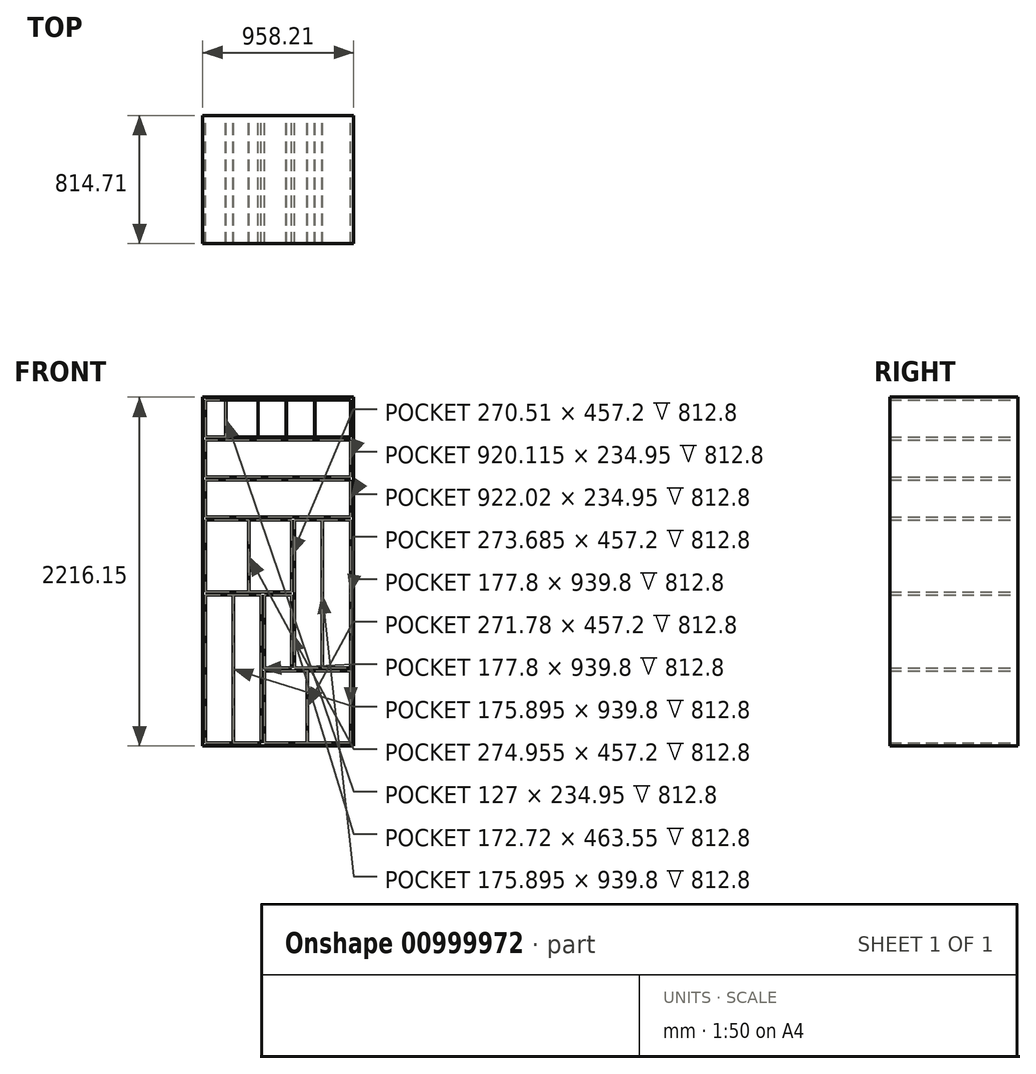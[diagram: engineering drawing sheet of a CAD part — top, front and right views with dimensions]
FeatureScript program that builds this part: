
annotation { "Feature Type Name" : "Feature", "Feature Type Description" : "" }
export const myFeature = defineFeature(function(context is Context, id is Id, definition is map)
    precondition{}
    {
        {
            var Q0;
            Q0=qCreatedBy(makeId("Front.planeOp"),FACE);
            var sketch = newSketch(context, id + "F0", { "sketchPlane" : qUnion([Q0])});
            skLineSegment(sketch, "E0.bottom", {"start": v(-388.07, -1236.82) * mm, "end": v(532.05, -1236.82) * mm});
            skLineSegment(sketch, "E0.left", {"start": v(-388.07, -1236.82) * mm, "end": v(-388.07, -436.72) * mm});
            skLineSegment(sketch, "E1.top", {"start": v(-388.07, 452.28) * mm, "end": v(533.95, 452.28) * mm});
            skLineSegment(sketch, "E1.left", {"start": v(-388.07, -436.72) * mm, "end": v(-388.07, 452.28) * mm});
            skLineSegment(sketch, "E1.right", {"start": v(533.95, -436.72) * mm, "end": v(533.95, 452.28) * mm});
            skLineSegment(sketch, "E2.bottom", {"start": v(-386.16, 941.23) * mm, "end": v(533.95, 941.23) * mm});
            skLineSegment(sketch, "E2.top", {"start": v(-386.16, 452.28) * mm, "end": v(533.95, 452.28) * mm});
            skLineSegment(sketch, "E2.left", {"start": v(-386.16, 941.23) * mm, "end": v(-386.16, 452.28) * mm});
            skLineSegment(sketch, "E2.right", {"start": v(533.95, 941.23) * mm, "end": v(533.95, 452.28) * mm});
            skLineSegment(sketch, "E3", {"start": v(-386.16, 706.28) * mm, "end": v(533.95, 706.28) * mm});
            skLineSegment(sketch, "E4", {"start": v(-388.07, 433.23) * mm, "end": v(533.95, 433.23) * mm});
            skLineSegment(sketch, "E5", {"start": v(-386.16, 687.23) * mm, "end": v(533.95, 687.23) * mm});
            skLineSegment(sketch, "E6", {"start": v(-282.66, 960.28) * mm, "end": v(533.95, 960.28) * mm});
            skLineSegment(sketch, "E7", {"start": v(533.95, 960.28) * mm, "end": v(533.95, 941.23) * mm});
            skLineSegment(sketch, "E8", {"start": v(-388.07, -1236.82) * mm, "end": v(-388.07, -1255.87) * mm});
            skLineSegment(sketch, "E9", {"start": v(-388.07, -1255.87) * mm, "end": v(532.05, -1255.87) * mm});
            skLineSegment(sketch, "E10.bottom", {"start": v(533.95, 960.28) * mm, "end": v(553, 960.28) * mm});
            skLineSegment(sketch, "E10.top", {"start": v(533.95, -1255.87) * mm, "end": v(553, -1255.87) * mm});
            skLineSegment(sketch, "E10.left", {"start": v(533.95, 960.28) * mm, "end": v(533.95, -1255.87) * mm});
            skLineSegment(sketch, "E10.right", {"start": v(553, 960.28) * mm, "end": v(553, -1255.87) * mm});
            skLineSegment(sketch, "E11.bottom", {"start": v(-282.66, 960.28) * mm, "end": v(-405.21, 960.28) * mm});
            skLineSegment(sketch, "E11.top", {"start": v(-342.2, -1255.87) * mm, "end": v(-405.21, -1255.87) * mm});
            skLineSegment(sketch, "E11.right", {"start": v(-405.21, 960.28) * mm, "end": v(-405.21, -1255.87) * mm});
            skLineSegment(sketch, "E12", {"start": v(-388.07, -297.02) * mm, "end": v(-32.47, -297.02) * mm});
            skLineSegment(sketch, "E13", {"start": v(-32.47, -297.02) * mm, "end": v(-32.47, -1236.82) * mm});
            skLineSegment(sketch, "E14", {"start": v(-388.07, -277.97) * mm, "end": v(-13.42, -277.97) * mm});
            skLineSegment(sketch, "E15", {"start": v(-13.42, -277.97) * mm, "end": v(-13.42, -1236.82) * mm});
            skLineSegment(sketch, "E16", {"start": v(-13.42, -779.62) * mm, "end": v(533.95, -779.62) * mm});
            skLineSegment(sketch, "E17", {"start": v(-13.42, -760.57) * mm, "end": v(533.95, -760.57) * mm});
            skLineSegment(sketch, "E18", {"start": v(260.27, -779.62) * mm, "end": v(260.27, -1236.82) * mm});
            skLineSegment(sketch, "E19", {"start": v(258.36, -779.62) * mm, "end": v(258.36, -1236.82) * mm});
            skLineSegment(sketch, "E20.bottom", {"start": v(533.95, -760.57) * mm, "end": v(178.35, -760.57) * mm});
            skLineSegment(sketch, "E20.top", {"start": v(533.95, 179.23) * mm, "end": v(178.35, 179.23) * mm});
            skLineSegment(sketch, "E20.left", {"start": v(533.95, -760.57) * mm, "end": v(533.95, 179.23) * mm});
            skLineSegment(sketch, "E20.right", {"start": v(178.35, -760.57) * mm, "end": v(178.35, 179.23) * mm});
            skLineSegment(sketch, "E21", {"start": v(159.3, -760.57) * mm, "end": v(159.3, 198.28) * mm});
            skLineSegment(sketch, "E22", {"start": v(159.3, 198.28) * mm, "end": v(533.95, 198.28) * mm});
            skLineSegment(sketch, "E23", {"start": v(-13.42, -277.97) * mm, "end": v(159.3, -277.97) * mm});
            skLineSegment(sketch, "E24", {"start": v(-32.47, -297.02) * mm, "end": v(159.3, -297.02) * mm});
            skLineSegment(sketch, "E25", {"start": v(159.3, 198.28) * mm, "end": v(-388.07, 198.28) * mm});
            skLineSegment(sketch, "E26", {"start": v(178.35, 179.23) * mm, "end": v(-388.07, 179.23) * mm});
            skLineSegment(sketch, "E27", {"start": v(-210.27, -297.02) * mm, "end": v(-210.27, -1236.82) * mm});
            skLineSegment(sketch, "E28", {"start": v(356.15, 179.23) * mm, "end": v(356.15, -760.57) * mm});
            skLineSegment(sketch, "E29", {"start": v(-212.17, -297.02) * mm, "end": v(-212.17, -1236.82) * mm});
            skLineSegment(sketch, "E30", {"start": v(354.25, 179.23) * mm, "end": v(354.25, -760.57) * mm});
            skLineSegment(sketch, "E31", {"start": v(-113.11, 179.23) * mm, "end": v(-113.11, -277.97) * mm});
            skLineSegment(sketch, "E32", {"start": v(-111.2, 179.23) * mm, "end": v(-111.2, -277.97) * mm});
            skLineSegment(sketch, "E33", {"start": v(-259.16, 941.23) * mm, "end": v(-259.16, 706.28) * mm});
            skLineSegment(sketch, "E34", {"start": v(-257.26, 941.23) * mm, "end": v(-257.26, 706.28) * mm});
            skLineSegment(sketch, "E35", {"start": v(-54.06, 941.23) * mm, "end": v(-54.06, 706.28) * mm});
            skLineSegment(sketch, "E36", {"start": v(-52.15, 941.23) * mm, "end": v(-52.15, 706.28) * mm});
            skLineSegment(sketch, "E37", {"start": v(125.65, 941.23) * mm, "end": v(125.65, 706.28) * mm});
            skPoint(sketch, "E37.startSnap0", {"position": v(125.65, 960.28) * mm});
            skLineSegment(sketch, "E38", {"start": v(127.55, 941.23) * mm, "end": v(127.55, 706.28) * mm});
            skLineSegment(sketch, "E39", {"start": v(305.35, 941.23) * mm, "end": v(305.35, 706.28) * mm});
            skLineSegment(sketch, "E40", {"start": v(307.26, 941.23) * mm, "end": v(307.26, 706.28) * mm});
            skLineSegment(sketch, "E41", {"start": v(532.05, -1236.82) * mm, "end": v(533.95, -1236.82) * mm});
            skLineSegment(sketch, "E42", {"start": v(532.05, -1255.87) * mm, "end": v(533.95, -1255.87) * mm});
            skSolve(sketch);
        }
        {
            var Q0;
            {var subQ8=sQuery(id+"F0.wireOp",EDGE,"E10.bottom");Q0=makeQuery(id+"F0.imprint","IMPRINT",FACE,{"disambiguationData":[TD([[makeQuery(id+"F0.imprint","IMPRINT",EDGE,{"derivedFrom":subQ8}),-1.0]])]});}
            var Q1;
            {var subQ9=sQuery(id+"F0.wireOp",EDGE,"E8");Q1=makeQuery(id+"F0.imprint","IMPRINT",FACE,{"disambiguationData":[TD([[makeQuery(id+"F0.imprint","IMPRINT",EDGE,{"derivedFrom":subQ9}),1.0]])]});}
            var Q2;
            {var subQ22=sQuery(id+"F0.wireOp",EDGE,"E0.left");Q2=makeQuery(id+"F0.imprint","IMPRINT",FACE,{"disambiguationData":[TD([[makeQuery(id+"F0.imprint","IMPRINT",EDGE,{"derivedFrom":subQ22}),1.0]])]});}
            var Q3;
            {var subQ5=sQuery(id+"F0.wireOp",EDGE,"E13");Q3=makeQuery(id+"F0.imprint","IMPRINT",FACE,{"disambiguationData":[TD([[makeQuery(id+"F0.imprint","IMPRINT",EDGE,{"derivedFrom":subQ5}),1.0]])]});}
            var Q4;
            {var subQ0=sQuery(id+"F0.wireOp",EDGE,"E16");var subQ1=sQuery(id+"F0.wireOp",EDGE,"E15");var subQ2=makeQuery(id+"F0.imprint","INTERSECT",VERTEX,{"derivedFrom":[subQ1,subQ0]});Q4=makeQuery(id+"F0.imprint","IMPRINT",FACE,{"disambiguationData":[TD([[makeQuery(id+"F0.imprint","IMPRINT",EDGE,{"disambiguationData":[TD([[subQ2,1.0]])],"derivedFrom":subQ1}),1.0]])]});}
            var Q5;
            {var subQ5=sQuery(id+"F0.wireOp",EDGE,"E20.right");Q5=makeQuery(id+"F0.imprint","IMPRINT",FACE,{"disambiguationData":[TD([[makeQuery(id+"F0.imprint","IMPRINT",EDGE,{"derivedFrom":subQ5}),1.0]])]});}
            var Q6;
            {var subQ0=sQuery(id+"F0.wireOp",EDGE,"E23");Q6=makeQuery(id+"F0.imprint","IMPRINT",FACE,{"disambiguationData":[TD([[makeQuery(id+"F0.imprint","IMPRINT",EDGE,{"derivedFrom":subQ0}),-1.0]])]});}
            var Q7;
            {var subQ1=sQuery(id+"F0.wireOp",EDGE,"E12");var subQ7=sQuery(id+"F0.wireOp",EDGE,"E1.left");var subQ8=makeQuery(id+"F0.imprint","INTERSECT",VERTEX,{"derivedFrom":[subQ7,subQ1]});Q7=makeQuery(id+"F0.imprint","IMPRINT",FACE,{"disambiguationData":[TD([[makeQuery(id+"F0.imprint","IMPRINT",EDGE,{"disambiguationData":[TD([[subQ8,-1.0]])],"derivedFrom":subQ7}),-1.0]])]});}
            var Q8;
            {var subQ4=sQuery(id+"F0.wireOp",EDGE,"E25");Q8=makeQuery(id+"F0.imprint","IMPRINT",FACE,{"disambiguationData":[TD([[makeQuery(id+"F0.imprint","IMPRINT",EDGE,{"derivedFrom":subQ4}),1.0]])]});}
            var Q9;
            {var subQ6=sQuery(id+"F0.wireOp",EDGE,"E22");Q9=makeQuery(id+"F0.imprint","IMPRINT",FACE,{"disambiguationData":[TD([[makeQuery(id+"F0.imprint","IMPRINT",EDGE,{"derivedFrom":subQ6}),-1.0]])]});}
            var Q10;
            {var subQ3=sQuery(id+"F0.wireOp",EDGE,"E1.top");Q10=makeQuery(id+"F0.imprint","IMPRINT",FACE,{"disambiguationData":[TD([[makeQuery(id+"F0.imprint","IMPRINT",EDGE,{"derivedFrom":subQ3}),-1.0]])]});}
            var Q11;
            {var subQ4=sQuery(id+"F0.wireOp",EDGE,"YxFC5J7E-RZ6B-db7r-RHHC-8dnZ2d5SKHM1");Q11=makeQuery(id+"F0.imprint","IMPRINT",FACE,{"disambiguationData":[TD([[makeQuery(id+"F0.imprint","IMPRINT",EDGE,{"derivedFrom":subQ4}),1.0]])]});}
            var Q12;
            {var subQ3=sQuery(id+"F0.wireOp",EDGE,"E3");Q12=makeQuery(id+"F0.imprint","IMPRINT",FACE,{"disambiguationData":[TD([[makeQuery(id+"F0.imprint","IMPRINT",EDGE,{"derivedFrom":subQ3}),-1.0]])]});}
            var Q13;
            {var subQ0=sQuery(id+"F0.wireOp",EDGE,"ODgAYMj3-4VNz-CoMQ-apJu-YLLPQxt6fLDd");Q13=makeQuery(id+"F0.imprint","IMPRINT",FACE,{"disambiguationData":[TD([[makeQuery(id+"F0.imprint","IMPRINT",EDGE,{"derivedFrom":subQ0}),1.0]])]});}
            var Q14;
            {var subQ0=sQuery(id+"F0.wireOp",EDGE,"mKUHKFXr-4xsX-OuSN-g5rI-rjY9IfRtsK5V");Q14=makeQuery(id+"F0.imprint","IMPRINT",FACE,{"disambiguationData":[TD([[makeQuery(id+"F0.imprint","IMPRINT",EDGE,{"derivedFrom":subQ0}),1.0]])]});}
            var Q15;
            {var subQ0=sQuery(id+"F0.wireOp",EDGE,"MaIjSTjV-kzmY-rfgm-6vS8-z4JOkT6mexGJ");Q15=makeQuery(id+"F0.imprint","IMPRINT",FACE,{"disambiguationData":[TD([[makeQuery(id+"F0.imprint","IMPRINT",EDGE,{"derivedFrom":subQ0}),1.0]])]});}
            var Q16;
            {var subQ0=sQuery(id+"F0.wireOp",EDGE,"gmUULXhB-zgWf-0V34-TWUs-H0ZNVVkrjR0e");Q16=makeQuery(id+"F0.imprint","IMPRINT",FACE,{"disambiguationData":[TD([[makeQuery(id+"F0.imprint","IMPRINT",EDGE,{"derivedFrom":subQ0}),1.0]])]});}
            var Q17;
            {var subQ0=sQuery(id+"F0.wireOp",EDGE,"E28");Q17=makeQuery(id+"F0.imprint","IMPRINT",FACE,{"disambiguationData":[TD([[makeQuery(id+"F0.imprint","IMPRINT",EDGE,{"derivedFrom":subQ0}),-1.0]])]});}
            var Q18;
            {var subQ0=sQuery(id+"F0.wireOp",EDGE,"E31");Q18=makeQuery(id+"F0.imprint","IMPRINT",FACE,{"disambiguationData":[TD([[makeQuery(id+"F0.imprint","IMPRINT",EDGE,{"derivedFrom":subQ0}),1.0]])]});}
            var Q19;
            {var subQ0=sQuery(id+"F0.wireOp",EDGE,"E27");Q19=makeQuery(id+"F0.imprint","IMPRINT",FACE,{"disambiguationData":[TD([[makeQuery(id+"F0.imprint","IMPRINT",EDGE,{"derivedFrom":subQ0}),-1.0]])]});}
            var Q20;
            {var subQ0=sQuery(id+"F0.wireOp",EDGE,"E18");Q20=makeQuery(id+"F0.imprint","IMPRINT",FACE,{"disambiguationData":[TD([[makeQuery(id+"F0.imprint","IMPRINT",EDGE,{"derivedFrom":subQ0}),-1.0]])]});}
            var Q21;
            {var subQ0=sQuery(id+"F0.wireOp",EDGE,"E33");Q21=makeQuery(id+"F0.imprint","IMPRINT",FACE,{"disambiguationData":[TD([[makeQuery(id+"F0.imprint","IMPRINT",EDGE,{"derivedFrom":subQ0}),1.0]])]});}
            var Q22;
            {var subQ0=sQuery(id+"F0.wireOp",EDGE,"E35");Q22=makeQuery(id+"F0.imprint","IMPRINT",FACE,{"disambiguationData":[TD([[makeQuery(id+"F0.imprint","IMPRINT",EDGE,{"derivedFrom":subQ0}),1.0]])]});}
            var Q23;
            {var subQ0=sQuery(id+"F0.wireOp",EDGE,"E37");Q23=makeQuery(id+"F0.imprint","IMPRINT",FACE,{"disambiguationData":[TD([[makeQuery(id+"F0.imprint","IMPRINT",EDGE,{"derivedFrom":subQ0}),1.0]])]});}
            var Q24;
            {var subQ0=sQuery(id+"F0.wireOp",EDGE,"E39");Q24=makeQuery(id+"F0.imprint","IMPRINT",FACE,{"disambiguationData":[TD([[makeQuery(id+"F0.imprint","IMPRINT",EDGE,{"derivedFrom":subQ0}),1.0]])]});}
            extrude(context, id + "F1", {"entities" : qUnion([Q0, Q1, Q2, Q3, Q4, Q5, Q6, Q7, Q8, Q9, Q10, Q11, Q12, Q13, Q14, Q15, Q16, Q17, Q18, Q19, Q20, Q21, Q22, Q23, Q24]), "depth" : 812.8 * mm, "offsetDistance" : 25.4 * mm});
        }
        {
            var Q0;
            Q0=makeQuery(id+"F1.opExtrude","CAP_FACE",FACE,{"disambiguationData":[OSD([sQuery(id+"F0.wireOp",EDGE,"E0.bottom"),sQuery(id+"F0.wireOp",EDGE,"E0.left"),sQuery(id+"F0.wireOp",EDGE,"E1.bottom"),sQuery(id+"F0.wireOp",EDGE,"E1.left"),sQuery(id+"F0.wireOp",EDGE,"31885118-5083-4cad-9ffd-2e04488de7a0"),sQuery(id+"F0.wireOp",EDGE,"acf1bfde-082d-452a-98a4-839e5ece4829"),sQuery(id+"F0.wireOp",EDGE,"a2540ab7-bdec-4d16-90f8-5cdeb7132558"),sQuery(id+"F0.wireOp",EDGE,"e4a99aba-132a-48d0-ba94-4c1ed472b65b"),sQuery(id+"F0.wireOp",EDGE,"3a9ddf20-e156-4800-a9b9-cce0476bb270"),sQuery(id+"F0.wireOp",EDGE,"83935ffd-2ab8-4473-b7a6-3f6ec7518ac8"),sQuery(id+"F0.wireOp",EDGE,"11cde19c-060c-4410-8b6d-4cab9da7d333"),sQuery(id+"F0.wireOp",EDGE,"E2.bottom"),sQuery(id+"F0.wireOp",EDGE,"E2.top"),sQuery(id+"F0.wireOp",EDGE,"E2.left"),sQuery(id+"F0.wireOp",EDGE,"526b48ae-27b5-4084-b20d-527d28139264"),sQuery(id+"F0.wireOp",EDGE,"E3"),sQuery(id+"F0.wireOp",EDGE,"d5c69c0a-5f5b-4855-964b-f854337130c0"),sQuery(id+"F0.wireOp",EDGE,"75838638-3cc9-401a-8bc6-d72bab6587cf"),sQuery(id+"F0.wireOp",EDGE,"7dcb5ebf-b62b-47f8-aec4-129f5508d045"),sQuery(id+"F0.wireOp",EDGE,"89e2364d-4218-4889-a458-1498f4e1db3f"),sQuery(id+"F0.wireOp",EDGE,"nheInwcn-Ck27-Lo5F-HrIv-6qlifbBUg3QC"),sQuery(id+"F0.wireOp",EDGE,"HUEE4SCl-0KTn-Riyo-HoFS-mRXdpzABmXYh"),sQuery(id+"F0.wireOp",EDGE,"xwl6UsIk-hOEg-Usse-HPrG-zQMZKOxZNE58"),sQuery(id+"F0.wireOp",EDGE,"E4"),sQuery(id+"F0.wireOp",EDGE,"YxFC5J7E-RZ6B-db7r-RHHC-8dnZ2d5SKHM1"),sQuery(id+"F0.wireOp",EDGE,"E5"),sQuery(id+"F0.wireOp",EDGE,"E6"),sQuery(id+"F0.wireOp",EDGE,"E9"),sQuery(id+"F0.wireOp",EDGE,"dQJq7JNr-q3OP-U5RH-nCup-Xf3UmPLMaNHK"),sQuery(id+"F0.wireOp",EDGE,"FNvmKpA7-qzfZ-yKGU-bboA-QHMhojb4ou9O"),sQuery(id+"F0.wireOp",EDGE,"mjj7kSNj-HMSZ-3xKI-QayC-YZH95KaO2xVR"),sQuery(id+"F0.wireOp",EDGE,"bMQWq9py-U7Ii-BlQB-WkTW-PvsZxb39EETB"),sQuery(id+"F0.wireOp",EDGE,"JBiFI1ma-0CFg-4mbK-GVQf-LbCcvvgmnVJ0"),sQuery(id+"F0.wireOp",EDGE,"UtRUjQvX-mNtP-4mV0-VuTZ-nqSPIabnDRkF"),sQuery(id+"F0.wireOp",EDGE,"IM0c7i3N-z1Es-PR3x-8nFU-a9EGMI1bVB26"),sQuery(id+"F0.wireOp",EDGE,"3SUdUadu-PXJz-n4kj-2MyB-lOrUpIntc1yE"),sQuery(id+"F0.wireOp",EDGE,"VNe765LQ-xWlj-d375-rxRR-i28GSOc6gKnw"),sQuery(id+"F0.wireOp",EDGE,"E10.bottom"),sQuery(id+"F0.wireOp",EDGE,"E10.top"),sQuery(id+"F0.wireOp",EDGE,"E10.left"),sQuery(id+"F0.wireOp",EDGE,"E10.right"),sQuery(id+"F0.wireOp",EDGE,"E11.bottom"),sQuery(id+"F0.wireOp",EDGE,"E11.top"),sQuery(id+"F0.wireOp",EDGE,"E11.right")])],"isStart":true});
            var sketch = newSketch(context, id + "F2", { "sketchPlane" : qUnion([Q0])});
            skLineSegment(sketch, "E43.bottom", {"start": v(-553, 960.28) * mm, "end": v(405.21, 960.28) * mm});
            skLineSegment(sketch, "E43.top", {"start": v(-553, -1255.87) * mm, "end": v(405.21, -1255.87) * mm});
            skLineSegment(sketch, "E43.left", {"start": v(-553, 960.28) * mm, "end": v(-553, -1255.87) * mm});
            skLineSegment(sketch, "E43.right", {"start": v(405.21, 960.28) * mm, "end": v(405.21, -1255.87) * mm});
            skSolve(sketch);
        }
        {
            var Q0;
            Q0 = qSketchRegion(id + "F2", true);
            extrude(context, id + "F3", {"entities" : qUnion([Q0]), "operationType" : NewBodyOperationType.ADD, "depth" : 1.9 * mm, "offsetDistance" : 25.4 * mm});
        }
    });
